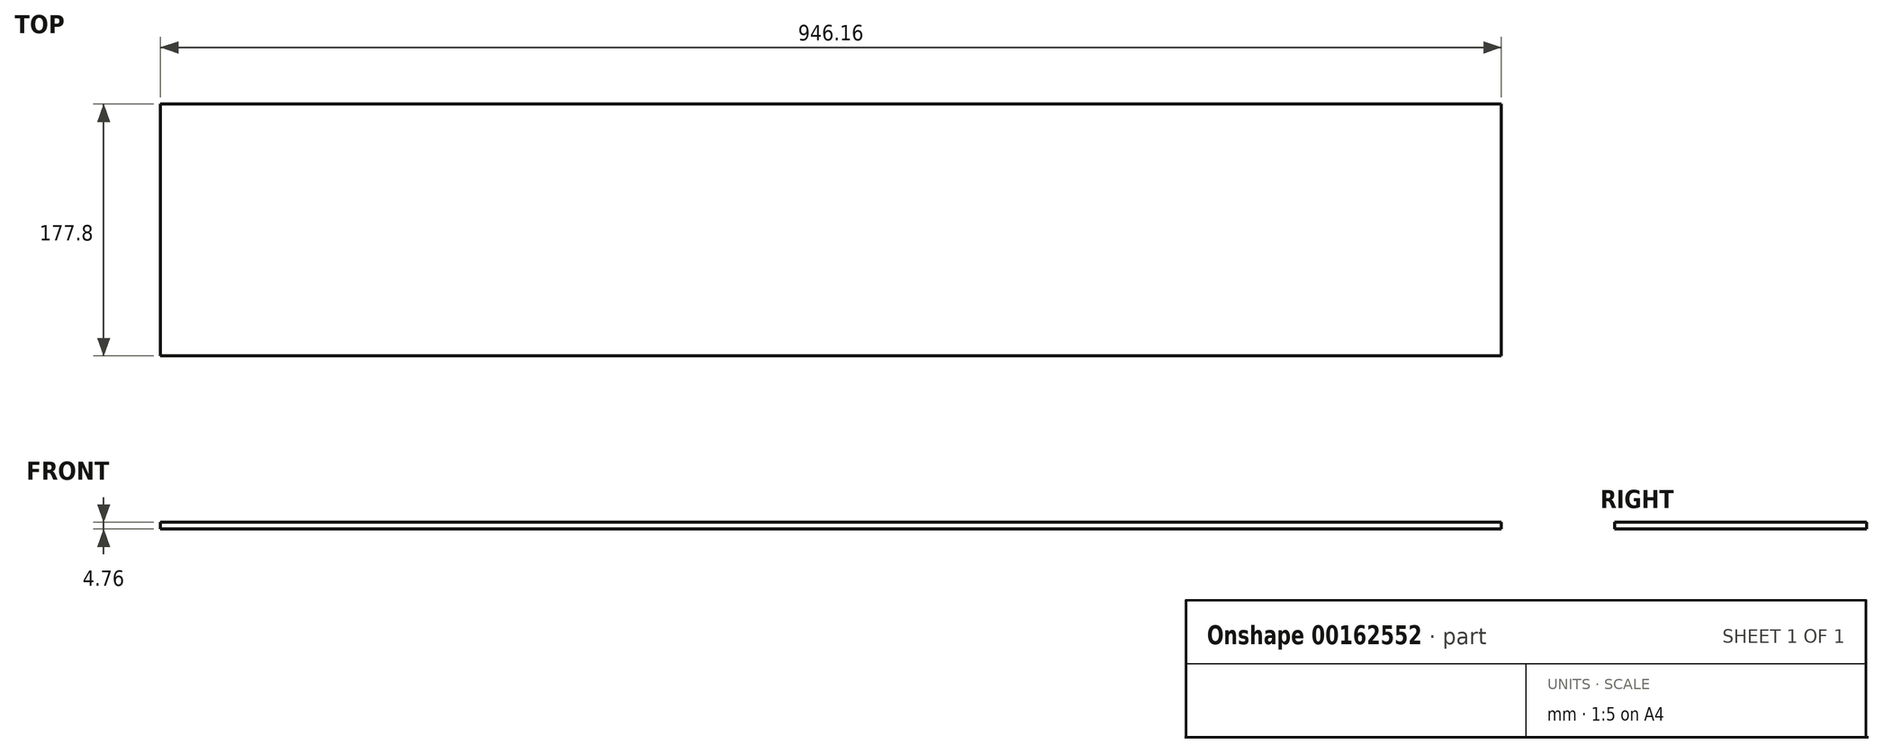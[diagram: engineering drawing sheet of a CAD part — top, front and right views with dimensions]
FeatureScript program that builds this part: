
annotation { "Feature Type Name" : "Feature", "Feature Type Description" : "" }
export const myFeature = defineFeature(function(context is Context, id is Id, definition is map)
    precondition{}
    {
        {
            var Q0;
            Q0=qCreatedBy(makeId("Top.planeOp"),FACE);
            var sketch = newSketch(context, id + "F0", { "sketchPlane" : qUnion([Q0])});
            skLineSegment(sketch, "E0.bottom", {"start": v(473.07, 88.9) * mm, "end": v(-473.08, 88.9) * mm});
            skLineSegment(sketch, "E0.top", {"start": v(473.08, -88.9) * mm, "end": v(-473.07, -88.9) * mm});
            skLineSegment(sketch, "E0.left", {"start": v(473.07, 88.9) * mm, "end": v(473.08, -88.9) * mm});
            skLineSegment(sketch, "E0.right", {"start": v(-473.08, 88.9) * mm, "end": v(-473.07, -88.9) * mm});
            skPoint(sketch, "E0.middle", {"position": v(0, 0) * mm});
            skSolve(sketch);
        }
        {
            var Q0;
            Q0=qSketchRegion(id+"F0",true);
            extrude(context, id + "F1", {"entities" : qUnion([Q0]), "depth" : 4.76 * mm});
        }
    });
